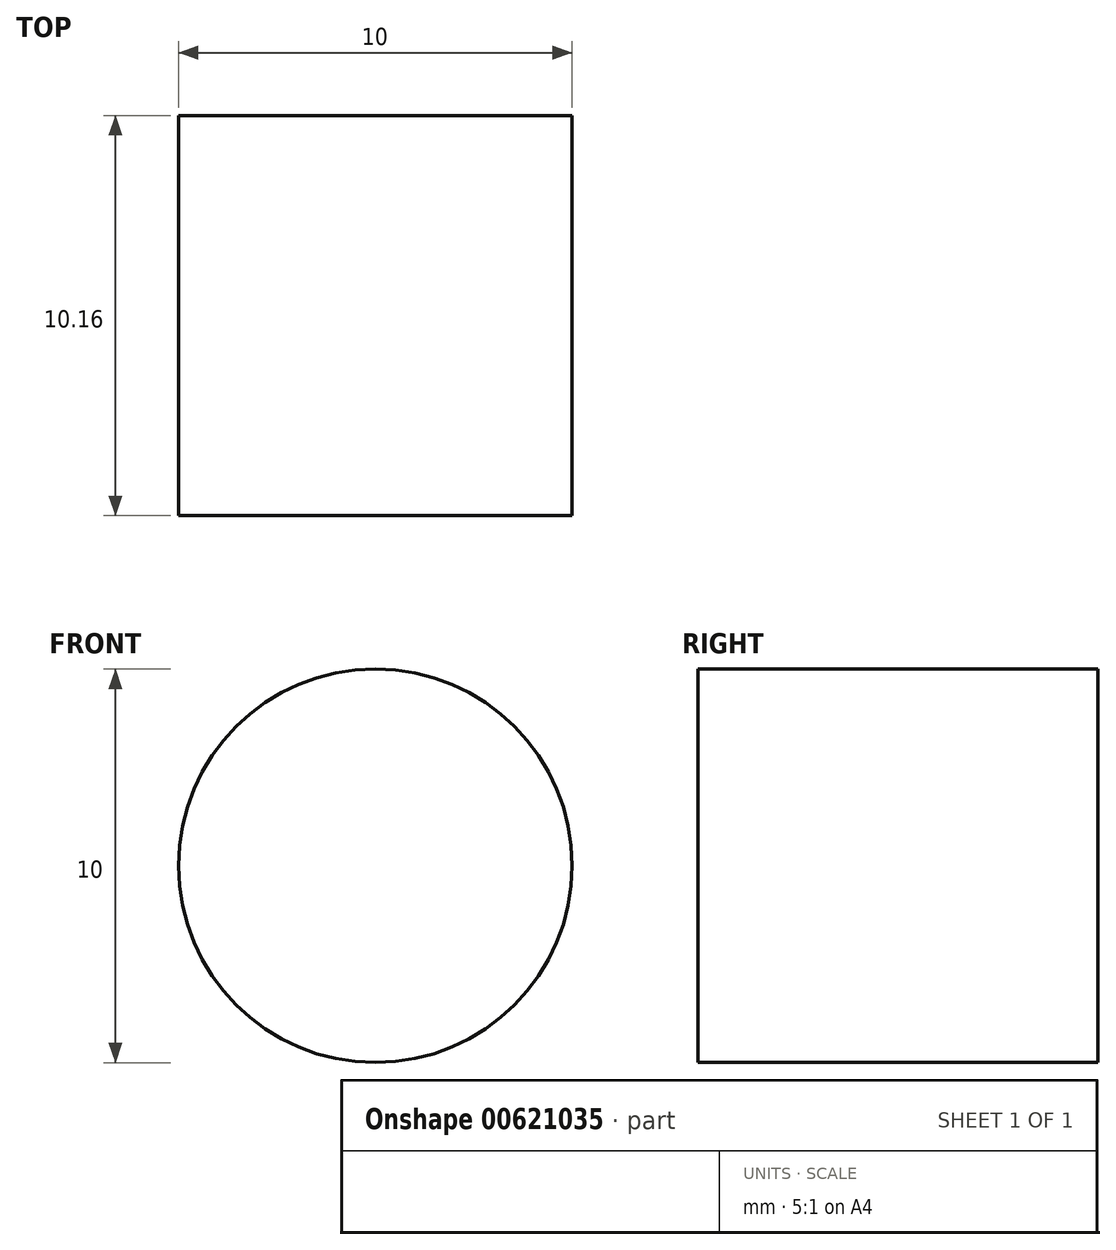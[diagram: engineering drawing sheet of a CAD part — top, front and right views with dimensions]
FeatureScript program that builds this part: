
annotation { "Feature Type Name" : "Feature", "Feature Type Description" : "" }
export const myFeature = defineFeature(function(context is Context, id is Id, definition is map)
    precondition{}
    {
        {
            var Q0;
            Q0=qCreatedBy(makeId("Front.planeOp"),FACE);
            var sketch = newSketch(context, id + "F0", { "sketchPlane" : qUnion([Q0])});
            skCircle(sketch, "E0", {"center": v(0, 8.3) * mm, "radius": 5 * mm});
            skSolve(sketch);
        }
        {
            var Q0;
            Q0 = qSketchRegion(id + "F0", true);
            extrude(context, id + "F1", {"entities" : qUnion([Q0]), "endBound" : BoundingType.SYMMETRIC, "oppositeDirection" : true, "depth" : 10.16 * mm, "offsetDistance" : 25.4 * mm});
        }
        {
            var Q0;
            Q0=makeQuery(id+"F1.opExtrude","SWEPT_BODY",BODY,{"disambiguationData":[OSD([sQuery(id+"F0.wireOp",EDGE,"E0")])]});
            var Q1;
            Q1=makeQuery(id+"F1.opExtrude","CAP_EDGE",EDGE,{"disambiguationData":[OSD([sQuery(id+"F0.wireOp",EDGE,"E0")])],"isStart":true});
            transform(context, id + "F2", {"entities" : qUnion([Q0]), "transformType" : TransformType.TRANSLATION_3D, "dx" : 23.1 * mm, "dy" : 41.4 * mm, "dz" : 12.2 * mm, "makeCopy" : false});
        }
    });
